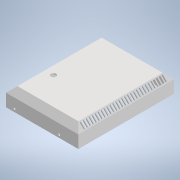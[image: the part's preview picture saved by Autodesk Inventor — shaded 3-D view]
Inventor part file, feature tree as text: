
AUTODESK INVENTOR PART (.ipt)
format: ipt  version: 2020.2 (Build 242310000, 310)  size: 453,632 bytes
history: native  units: in
note: dims shown in document units (in); Inventor stores cm internally (conversion verified against a paired STEP export)
features: sketch x10, hole x9, other x7, reference x4, fillet x2, extrude x1
ambient origin geometry x8: Origin, YZ Plane, XZ Plane, XY Plane, X Axis, Y Axis, Z Axis, Center Point
bodies: Solid1 (feature_tree)
feature tree (33):
  other  "Back_Case.ipt"
  extrude  "Extrusion1"  Depth=0.25in
  hole  "Hole1"  [1 undecoded]
  hole  "Hole2"  [1 undecoded]
  hole  "Hole3"  [1 undecoded]
  hole  "Hole4"  [1 undecoded]
  hole  "Hole7"  [1 undecoded]
  hole  "Hole8"  [1 undecoded]
  hole  "Hole9"  [1 undecoded]
  fillet  "Fillet1"  Radius=0.25in
  fillet  "Fillet2"  Radius=1.686in
  hole  "Hole10"  [1 undecoded]
  hole  "Hole11"  [1 undecoded]
  other  "Vented Case::Back_Case.ipt"
  other  "TaggingFeature1"
  sketch  "Sketch1"  dims[d0=0.3937in d1=0.25in]
  reference  "Reference1"
  reference  "Reference2"
  reference  "Reference3"
  reference  "Reference4"
  sketch  "Sketch2"  dims[d2=0.25in d3=0.25in]
  sketch  "Sketch3"  dims[d4=0.25in d5=0.25in d6=0.0in]
  sketch  "Sketch4"  dims[d7=0.0968in d8=0.2in d9=0.375in d10=0.25in d11=0.5635in d12=0.2in d13=0.0in]
  sketch  "Sketch5"  dims[d14=0.0968in d15=0.2in d16=0.375in d17=0.25in d18=0.5635in d19=0.2in d20=0.0in]
  sketch  "Sketch8"  dims[d21=0.0968in d22=0.2in d23=0.375in d24=0.25in d25=0.5635in d26=0.2in d27=0.0in]
  sketch  "Sketch9"  dims[d28=0.0968in d29=0.2in d30=0.375in d31=0.25in d32=0.5635in d33=0.2in d34=0.0in d53=0.25in]
  sketch  "Sketch10"  dims[d54=2.0in]
  sketch  "Sketch11"  dims[d55=0.177in d56=0.315in d57=0.37in d58=0.25in d59=90.0deg d60=0.465in d61=0.0in d62=2.0in]
  sketch  "Sketch12"  dims[d63=0.25in d64=0.177in d65=0.315in d66=0.37in d67=0.25in d68=90.0deg d69=0.465in d70=0.0in d71=0.42in d72=0.315in d73=0.37in d74=0.25in d75=90.0deg d76=0.465in d77=0.0in d78=0.0312in d79=0.0625in d80=0.735in d81=0.25in d82=0.177in d83=0.315in d84=0.37in d85=0.25in d86=90.0deg d87=0.465in d88=0.0in d89=1.686in d90=0.25in d91=0.177in d92=0.315in d93=0.37in d94=0.25in d95=90.0deg d96=0.465in d97=0.0in]
  parser-record x1  (decoder bookkeeping rows leaked as tree rows — omitted from the tree; the rows remain in map.json)
  other  "Back_Case.iam"
  other  "raspberrypi_3_stripped:1"
  other  "Raspberry Pi 31:1"
note: 9 required parameter values undecoded (feature->parameter linkage not recoverable at this tier; creation-order binding heuristic only, values carry confidence <= 0.55)
note: 1 file-system path scrubbed to <path> (originals preserved in map.json)
